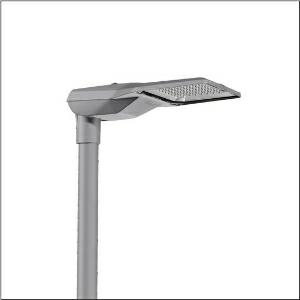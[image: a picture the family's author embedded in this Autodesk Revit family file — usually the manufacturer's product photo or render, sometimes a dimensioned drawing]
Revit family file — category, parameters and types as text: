
# Revit family: streetlight_sl_21_midi___st1_0ab_5xe3m33s08mb_fd22
name_source: partatom
category: Lighting Fixtures
units: mm (PartAtom-declared; Revit-internal decimal feet)

## family parameters
Cut with Voids When Loaded = No
Host = Face
Light Source = No
Part Type = Normal
Room Calculation Point = No
Round Connector Dimension = Use Diameter
Shared = No

## types (1)
- --- (1 x LED, 16080 lm, 136 W, 3000K)
    Apparent Load = 136 VA
    CIE Flux Codes = 38 73 97 100 100
    Color Rendering = 70
    Color Temperature = 3000K
    Default Elevation = 1800 mm
    Description = Streetlight SL 21 midi, mast luminaire, primary light control with lens, of PMMA, primary optical cover: cover, of toughened safety glass, transparent, light distribution: ST1.0aB, light emission: direct distribution, primary light characteristic: asymmetric, installation type: side-entry, post-top, LED, High Power LED, rated luminous flux: 16.080lm, luminous efficacy: 118lm/W, light colour: 730, colour temperature: 3000K, control gear: D4i, control: flexible luminous flux parameterisation, time-dependent luminous flux control, constant luminous flux control, overheat protection, pre-setting: logarithmic dimming characteristic, mains connection: 230..240V, AC, 50/60Hz, start of lifetime: 136W, end of service life: 142W, reduction: 61W, luminaire housing, of diecast aluminium, powder-coated, SITECO metallic grey (DB 702S), corrosivity category C5 high according to DIN EN ISO 12944, please order mast flange separately, inclination adjustable: 0°, 5°, 10°, 15°, sealing non-destructively replaceable, multi-level sealing system, length: 644mm, width: 335mm, height: 110mm, mast flange for spigot size: 42mm (side-entry): 5XC10008XM4, 60/48mm (side-entry/post-top): 5XC10108XM2, 76/60mm (side-entry/post-top): 5XC10108XM1, mounting height: 4..8m, Smart Interface above, protection rating (complete): IP66, insulation class (complete): insulation class II (safety insulation), certification: CE, ENEC, ENEC+, VDE, impact resistance: IK10, permissible operating ambient temperature for outdoor applications: -40..+50°C, standard-compliant lighting for roads and squares, packaging unit: 1 piece

Light Distribution: ST1.0aB
    Height = 111 mm
    Lamp = 1 x LED
    Lamp Light Flux = 16080 lm
    Lamp Power = 136 W
    Lamp count = 1
    Length = 644 mm
    Luminous efficacy = 118 lm/W
    Manufacturer = Siteco
    ModVariant = No
    Model = 5XE3M33S08MB
    Number of Poles = 1
    OnlyDefault = Yes
    Power Factor = 1
    Product Name = Streetlight SL 21 midi | ST1.0aB
    Product group = mast luminaire | pylon top
    ProductGroupID = 6100
    Protection Class = Protection class II
    Protection Degree = IP 66
    RLX_Detail_Level = 1
    RLX_Emergency_Light_Flux = 0 lm
    RLX_Emergency_Type = 0
    RLX_Emergency_Type_DB = No
    RlxData = <blob elided: 26845 chars, md5=0c22c374>
    Socket = socket
    Standby Power = 0 W
    System Light Flux = 16081 lm
    System Power = 136 W
    Type Comments = factory setting: luminous flux: 100 % | dim-lin: 254 | 695 mA
    Type Image = l_1004302.jpg
    URL = http://relux.com
    VarID = @adj_180385
    Voltage = 0 V
    Weight = 0.00 kg
    Width = 336 mm

## geometry (parser evidence)
native form markers: Blend x4, Sweep x10
no freeform markers — native parametric forms only
